# Revit family: TOP31
name_source: partatom
category: Plumbing Fixtures
revit_build: Autodesk Revit 2015 (Build: 20140905_0730(x64)
units: mm (PartAtom-declared; Revit-internal decimal feet)

## types (4) — shared parameters
Aluminum = Aluminum
Glass = Glass
Manufacturer = SanSwiss
Model = TOP31
Profile = Profile
Seal = Seal
Type Comments = TOP LINE
URL = http://www.sanswiss.com

## per-type parameters (varying)
| type | A | B | C |
| 900 | 900 mm  [stored 2.95276 ft] | 258 mm  [stored 0.846457 ft] | 642 mm  [stored 2.1063 ft] |
| 1400 | 1400 mm  [stored 4.59318 ft] | 458 mm | 942 mm  [stored 3.09055 ft] |
| 1200 | 1200 mm | 358 mm  [stored 1.17454 ft] | 842 mm  [stored 2.76247 ft] |
| 1000 | 1000 mm  [stored 3.28084 ft] | 258 mm  [stored 0.846457 ft] | 742 mm  [stored 2.43438 ft] |

note: [stored X ft] marks values corroborated as IEEE doubles in the binary element streams (Revit-internal decimal feet)

## geometry (parser evidence)
native form markers: Blend x4, Sweep x10
no freeform markers — native parametric forms only
